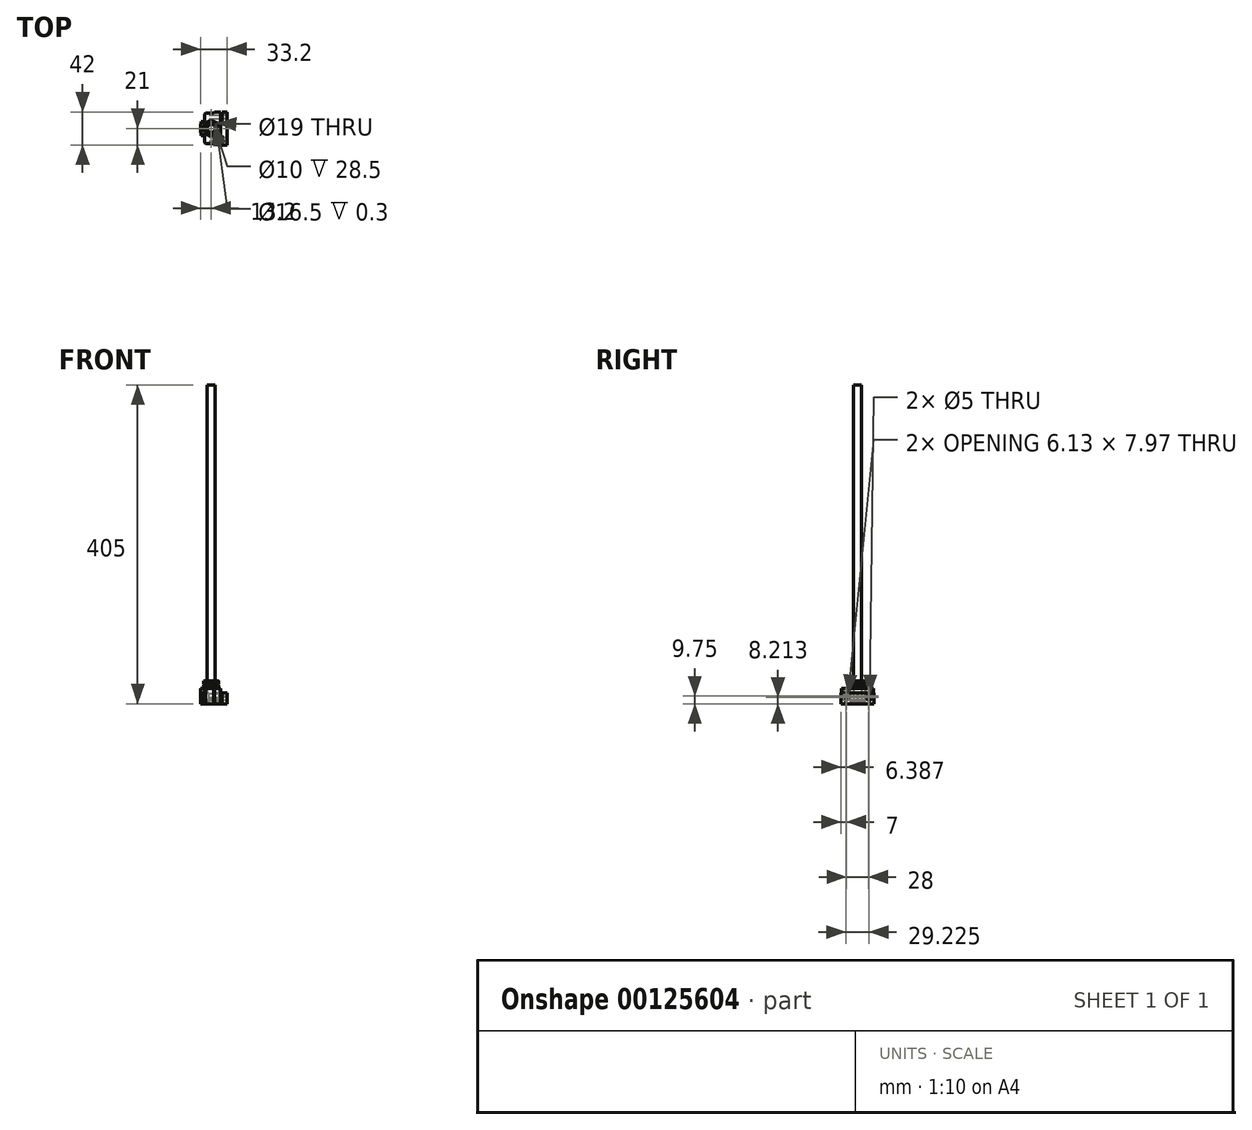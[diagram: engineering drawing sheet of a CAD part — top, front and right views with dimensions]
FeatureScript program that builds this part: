
annotation { "Feature Type Name" : "Feature", "Feature Type Description" : "" }
export const myFeature = defineFeature(function(context is Context, id is Id, definition is map)
    precondition{}
    {
        {
            var Q0;
            Q0=qCreatedBy(makeId("Top.planeOp"),FACE);
            var sketch = newSketch(context, id + "F0", { "sketchPlane" : qUnion([Q0])});
            skLineSegment(sketch, "E0", {"start": v(20, 21) * mm, "end": v(20, -21) * mm});
            skLineSegment(sketch, "E1", {"start": v(20, -21) * mm, "end": v(14, -21) * mm});
            skLineSegment(sketch, "E2", {"start": v(14, -21) * mm, "end": v(14, -8.9) * mm});
            skLineSegment(sketch, "E3", {"start": v(14, -8.9) * mm, "end": v(-12.8, -8.9) * mm});
            skLineSegment(sketch, "E4", {"start": v(-12.8, -8.9) * mm, "end": v(-12.8, -0.5) * mm});
            skLineSegment(sketch, "E5", {"start": v(-12.8, 8.9) * mm, "end": v(14, 8.9) * mm});
            skLineSegment(sketch, "E6", {"start": v(14, 8.9) * mm, "end": v(14, 21) * mm});
            skLineSegment(sketch, "E7", {"start": v(14, 21) * mm, "end": v(20, 21) * mm});
            skArc(sketch, "E8", {"start": v(-4.97, -0.5) * mm, "mid": v(5, 0) * mm, "end": v(-4.97, 0.5) * mm});
            skPoint(sketch, "E9", {"position": v(-12.8, 0) * mm});
            skPoint(sketch, "E10", {"position": v(20, 0) * mm});
            skLineSegment(sketch, "E11", {"start": v(-12.8, -0.5) * mm, "end": v(-4.97, -0.5) * mm});
            skLineSegment(sketch, "E12", {"start": v(-12.8, 0) * mm, "end": v(20, 0) * mm, "construction": true});
            skLineSegment(sketch, "E13.MirrorCS", {"start": v(-12.8, 0.5) * mm, "end": v(-4.97, 0.5) * mm});
            skLineSegment(sketch, "E14.trimOffspring", {"start": v(-12.8, 0.5) * mm, "end": v(-12.8, 8.9) * mm});
            skSolve(sketch);
        }
        {
            var Q0;
            Q0 = qSketchRegion(id + "F0", true);
            extrude(context, id + "F1", {"entities" : qUnion([Q0]), "depth" : 13.8 * mm});
        }
        {
            var Q0;
            Q0=makeQuery(id+"F1.opExtrude","SWEPT_FACE",FACE,{"disambiguationData":[OSD([sQuery(id+"F0.wireOp",EDGE,"E6")])]});
            var sketch = newSketch(context, id + "F2", { "sketchPlane" : qUnion([Q0])});
            skCircle(sketch, "E15", {"center": v(-14.95, 6.9) * mm, "radius": 2.75 * mm});
            skCircle(sketch, "E16", {"center": v(14.95, 6.9) * mm, "radius": 2.75 * mm});
            skSolve(sketch);
        }
        {
            var Q0;
            Q0=makeQuery(id+"F2.imprint","IMPRINT",FACE,{"disambiguationData":[TD([[makeQuery(id+"F2.imprint","IMPRINT",EDGE,{"derivedFrom":sQuery(id+"F2.wireOp",EDGE,"E15")}),1.0]])]});
            var Q1;
            Q1=makeQuery(id+"F2.imprint","IMPRINT",FACE,{"disambiguationData":[TD([[makeQuery(id+"F2.imprint","IMPRINT",EDGE,{"derivedFrom":sQuery(id+"F2.wireOp",EDGE,"E16")}),1.0]])]});
            extrude(context, id + "F3", {"entities" : qUnion([Q0, Q1]), "operationType" : NewBodyOperationType.REMOVE, "endBound" : BoundingType.THROUGH_ALL, "oppositeDirection" : true, "depth" : 25 * mm});
        }
        {
            var Q0;
            Q0=qCreatedBy(makeId("Top.planeOp"),FACE);
            var sketch = newSketch(context, id + "F4", { "sketchPlane" : qUnion([Q0])});
            skLineSegment(sketch, "E17", {"start": v(12.3, 20.4) * mm, "end": v(12.3, -20.4) * mm});
            skLineSegment(sketch, "E18", {"start": v(12.3, -20.4) * mm, "end": v(4.3, -20.4) * mm});
            skLineSegment(sketch, "E19", {"start": v(4.3, -20.4) * mm, "end": v(3.05, -19.15) * mm});
            skLineSegment(sketch, "E20", {"start": v(3.05, -19.15) * mm, "end": v(-7.05, -19.15) * mm});
            skLineSegment(sketch, "E21", {"start": v(-7.05, -19.15) * mm, "end": v(-8.2, -18) * mm});
            skLineSegment(sketch, "E22", {"start": v(-8.2, -18) * mm, "end": v(-8.2, -10) * mm});
            skLineSegment(sketch, "E23", {"start": v(-8.2, -10) * mm, "end": v(-13.2, -5.25) * mm});
            skLineSegment(sketch, "E24", {"start": v(-13.2, -5.25) * mm, "end": v(-13.2, 5.25) * mm});
            skLineSegment(sketch, "E25", {"start": v(-13.2, 5.25) * mm, "end": v(-8.2, 10) * mm});
            skLineSegment(sketch, "E26", {"start": v(-8.2, 10) * mm, "end": v(-8.2, 18) * mm});
            skLineSegment(sketch, "E27", {"start": v(-8.2, 18) * mm, "end": v(-7.05, 19.15) * mm});
            skLineSegment(sketch, "E28", {"start": v(-7.05, 19.15) * mm, "end": v(3.05, 19.15) * mm});
            skLineSegment(sketch, "E29", {"start": v(3.05, 19.15) * mm, "end": v(4.3, 20.4) * mm});
            skLineSegment(sketch, "E30", {"start": v(4.3, 20.4) * mm, "end": v(12.3, 20.4) * mm});
            skLineSegment(sketch, "E31", {"start": v(-13.2, 0) * mm, "end": v(12.3, 0) * mm, "construction": true});
            skCircle(sketch, "E32", {"center": v(0, 0) * mm, "radius": 9.5 * mm});
            skCircle(sketch, "E33", {"center": v(0, 0) * mm, "radius": 5 * mm});
            skCircle(sketch, "E34", {"center": v(0, 0) * mm, "radius": 8.25 * mm});
            skSolve(sketch);
        }
        {
            var Q0;
            Q0=makeQuery(id+"F4.imprint","IMPRINT",FACE,{"disambiguationData":[TD([[makeQuery(id+"F4.imprint","IMPRINT",EDGE,{"derivedFrom":sQuery(id+"F4.wireOp",EDGE,"E17")}),-1.0]])]});
            extrude(context, id + "F5", {"entities" : qUnion([Q0]), "depth" : 19.5 * mm});
        }
        {
            var Q0;
            Q0=makeQuery(id+"F4.imprint","IMPRINT",FACE,{"disambiguationData":[TD([[makeQuery(id+"F4.imprint","IMPRINT",EDGE,{"derivedFrom":sQuery(id+"F4.wireOp",EDGE,"E32")}),1.0]])]});
            extrude(context, id + "F6", {"entities" : qUnion([Q0]), "depth" : 29 * mm});
        }
        {
            var Q0;
            Q0=makeQuery(id+"F4.imprint","IMPRINT",FACE,{"disambiguationData":[TD([[makeQuery(id+"F4.imprint","IMPRINT",EDGE,{"derivedFrom":sQuery(id+"F4.wireOp",EDGE,"E33")}),-1.0]])]});
            extrude(context, id + "F7", {"entities" : qUnion([Q0]), "operationType" : NewBodyOperationType.ADD, "depth" : 28.5 * mm, "hasSecondDirection" : true, "secondDirectionOppositeDirection" : false, "secondDirectionDepth" : .5 * mm});
        }
        {
            var Q0;
            Q0=qCreatedBy(makeId("Front.planeOp"),FACE);
            var sketch = newSketch(context, id + "F8", { "sketchPlane" : qUnion([Q0])});
            skLineSegment(sketch, "E35.0", {"start": v(-9.5, 29) * mm, "end": v(9.5, 29) * mm, "construction": true});
            skLineSegment(sketch, "E36.bottom", {"start": v(-9.5, 25.5) * mm, "end": v(-8.5, 25.5) * mm});
            skLineSegment(sketch, "E36.top", {"start": v(-9.5, 24.25) * mm, "end": v(-8.5, 24.25) * mm});
            skLineSegment(sketch, "E36.left", {"start": v(-9.5, 25.5) * mm, "end": v(-9.5, 24.25) * mm});
            skLineSegment(sketch, "E36.right", {"start": v(-8.5, 25.5) * mm, "end": v(-8.5, 24.25) * mm});
            skLineSegment(sketch, "E37.bottom", {"start": v(-9.5, 3.5) * mm, "end": v(-8.5, 3.5) * mm});
            skLineSegment(sketch, "E37.top", {"start": v(-9.5, 4.75) * mm, "end": v(-8.5, 4.75) * mm});
            skLineSegment(sketch, "E37.left", {"start": v(-9.5, 3.5) * mm, "end": v(-9.5, 4.75) * mm});
            skLineSegment(sketch, "E37.right", {"start": v(-8.5, 3.5) * mm, "end": v(-8.5, 4.75) * mm});
            skLineSegment(sketch, "E38", {"start": v(-9.5, 14.5) * mm, "end": v(9.5, 14.5) * mm, "construction": true});
            skLineSegment(sketch, "E39", {"start": v(-9.5, 14.5) * mm, "end": v(-9.5, 24.25) * mm, "construction": true});
            skLineSegment(sketch, "E40", {"start": v(-9.5, 14.5) * mm, "end": v(-9.5, 4.75) * mm, "construction": true});
            skLineSegment(sketch, "E41", {"start": v(0, 0) * mm, "end": v(0, 14.5) * mm, "construction": true});
            skSolve(sketch);
        }
        {
            var Q0;
            Q0=makeQuery(id+"F8.imprint","IMPRINT",FACE,{"disambiguationData":[TD([[makeQuery(id+"F8.imprint","IMPRINT",EDGE,{"derivedFrom":sQuery(id+"F8.wireOp",EDGE,"E36.bottom")}),-1.0]])]});
            var Q1;
            Q1=makeQuery(id+"F8.imprint","IMPRINT",FACE,{"disambiguationData":[TD([[makeQuery(id+"F8.imprint","IMPRINT",EDGE,{"derivedFrom":sQuery(id+"F8.wireOp",EDGE,"E37.bottom")}),1.0]])]});
            var Q2;
            Q2=sQuery(id+"F8.wireOp",EDGE,"E41");
            revolve(context, id + "F9", {"operationType" : NewBodyOperationType.REMOVE, "entities" : qUnion([Q0, Q1]), "axis" : qUnion([Q2]), "revolveType" : RevolveType.FULL, "oppositeDirection" : true});
        }
        {
            var Q0;
            Q0=makeQuery(id+"F6.opExtrude","CAP_EDGE",EDGE,{"disambiguationData":[OSD([sQuery(id+"F4.wireOp",EDGE,"E32")])],"isStart":false});
            var Q1;
            Q1=makeQuery(id+"F6.opExtrude","CAP_EDGE",EDGE,{"disambiguationData":[OSD([sQuery(id+"F4.wireOp",EDGE,"E34")])],"isStart":false});
            var Q2;
            Q2=makeQuery(id+"F9.boolean.opBoolean","COPY",EDGE,{"derivedFrom":makeQuery(id+"F9.opRevolve","SWEPT_EDGE",EDGE,{"disambiguationData":[OSD([sQuery(id+"F8.wireOp",EDGE,"E36.top"),sQuery(id+"F8.wireOp",EDGE,"E36.left")])]})});
            var Q3;
            Q3=makeQuery(id+"F9.boolean.opBoolean","COPY",EDGE,{"derivedFrom":makeQuery(id+"F9.opRevolve","SWEPT_EDGE",EDGE,{"disambiguationData":[OSD([sQuery(id+"F8.wireOp",EDGE,"E36.bottom"),sQuery(id+"F8.wireOp",EDGE,"E36.left")])]})});
            var Q4;
            Q4=makeQuery(id+"F9.boolean.opBoolean","COPY",EDGE,{"derivedFrom":makeQuery(id+"F9.opRevolve","SWEPT_EDGE",EDGE,{"disambiguationData":[OSD([sQuery(id+"F8.wireOp",EDGE,"E37.bottom"),sQuery(id+"F8.wireOp",EDGE,"E37.left")])]})});
            var Q5;
            Q5=makeQuery(id+"F9.boolean.opBoolean","COPY",EDGE,{"derivedFrom":makeQuery(id+"F9.opRevolve","SWEPT_EDGE",EDGE,{"disambiguationData":[OSD([sQuery(id+"F8.wireOp",EDGE,"E37.top"),sQuery(id+"F8.wireOp",EDGE,"E37.left")])]})});
            var Q6;
            Q6=makeQuery(id+"F6.opExtrude","CAP_EDGE",EDGE,{"disambiguationData":[OSD([sQuery(id+"F4.wireOp",EDGE,"E32")])],"isStart":true});
            var Q7;
            Q7=makeQuery(id+"F6.opExtrude","CAP_EDGE",EDGE,{"disambiguationData":[OSD([sQuery(id+"F4.wireOp",EDGE,"E34")])],"isStart":true});
            chamfer(context, id + "F10", {"entities" : qUnion([Q0, Q1, Q2, Q3, Q4, Q5, Q6, Q7]), "width" : .2 * mm, "tangentPropagation" : true});
        }
        {
            var Q0;
            Q0=makeQuery(id+"F5.opExtrude","SWEPT_FACE",FACE,{"disambiguationData":[OSD([sQuery(id+"F4.wireOp",EDGE,"E26")])]});
            var sketch = newSketch(context, id + "F11", { "sketchPlane" : qUnion([Q0])});
            skCircle(sketch, "E42", {"center": v(-14, 9.75) * mm, "radius": 2.5 * mm});
            skPoint(sketch, "E42.centerSnap0", {"position": v(-14, 19.5) * mm});
            skPoint(sketch, "E42.centerSnap1", {"position": v(-18, 9.75) * mm});
            skCircle(sketch, "E43", {"center": v(14, 9.75) * mm, "radius": 2.5 * mm});
            skSolve(sketch);
        }
        {
            var Q0;
            Q0=makeQuery(id+"F11.imprint","IMPRINT",FACE,{"disambiguationData":[TD([[makeQuery(id+"F11.imprint","IMPRINT",EDGE,{"derivedFrom":sQuery(id+"F11.wireOp",EDGE,"E43")}),1.0]])]});
            var Q1;
            Q1=makeQuery(id+"F11.imprint","IMPRINT",FACE,{"disambiguationData":[TD([[makeQuery(id+"F11.imprint","IMPRINT",EDGE,{"derivedFrom":sQuery(id+"F11.wireOp",EDGE,"E42")}),1.0]])]});
            extrude(context, id + "F12", {"entities" : qUnion([Q0, Q1]), "operationType" : NewBodyOperationType.REMOVE, "endBound" : BoundingType.THROUGH_ALL, "oppositeDirection" : true, "depth" : 25 * mm});
        }
        {
            var Q0;
            Q0=makeQuery(id+"F4.imprint","IMPRINT",FACE,{"disambiguationData":[TD([[makeQuery(id+"F4.imprint","IMPRINT",EDGE,{"derivedFrom":sQuery(id+"F4.wireOp",EDGE,"E33")}),1.0]])]});
            extrude(context, id + "F13", {"entities" : qUnion([Q0]), "depth" : 405 * mm});
        }
    });
